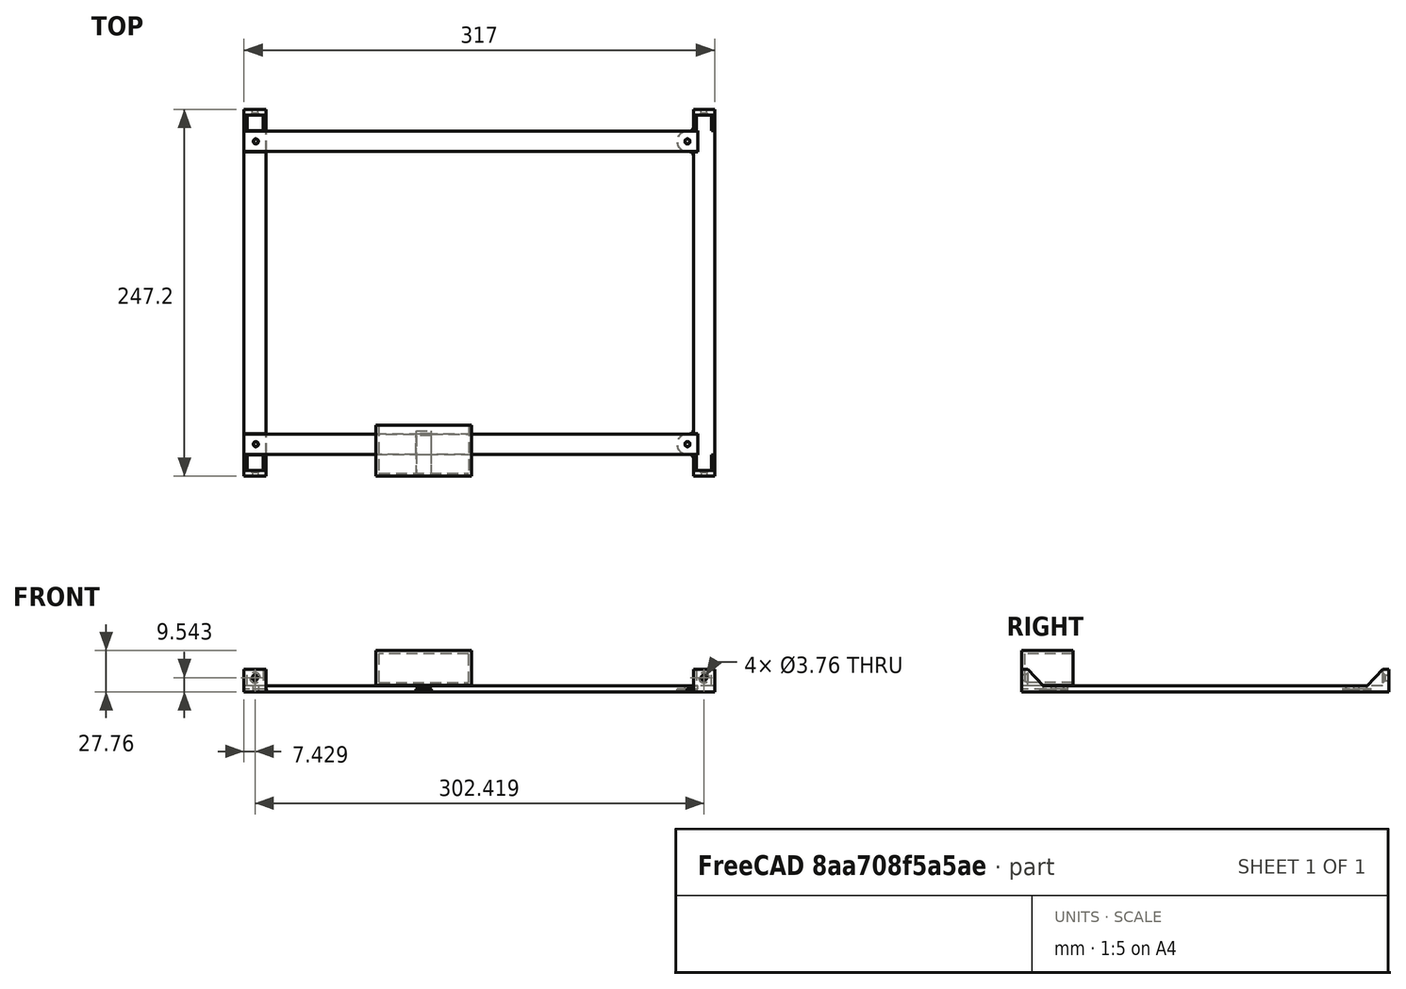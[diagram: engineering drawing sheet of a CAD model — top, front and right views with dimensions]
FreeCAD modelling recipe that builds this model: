
FCSTD DOCUMENT  (FreeCAD 1.0R39319 (Git))
Label: mounting
License: All rights reserved
LicenseURL: https://en.wikipedia.org/wiki/All_rights_reserved
objects: Sketcher::SketchObject×27, PartDesign::Pad×17, PartDesign::Hole×9, PartDesign::Body×5, TechDraw::DrawProjGroupItem×4, TechDraw::DrawViewDimension×3, PartDesign::Plane×2, PartDesign::Mirrored×2, Spreadsheet::Sheet×1, PartDesign::Pocket×1, TechDraw::DrawSVGTemplate×1, TechDraw::DrawProjGroup×1, TechDraw::DrawPage×1
note: 152 computed .brp shape members not serialized (recipe doc carries the construction recipe); baked Part::Feature solids carry a one-line shape summary decoded from their .brp

FEATURE [Spreadsheet::Sheet] Spreadsheet  label="Dimensions"
  cells = A1='Property; B1='value (mm); C1='description (left/right relative to FRONT OF SCREEN); A2='frame_inner_width; B2(frame_inner_width)=317.5; C2='Width of the inside of the frame, ie, width of the glass and matting.; A3='frame_inner_height; B3(frame_inner_height)=247.7; C3='Height of the inside of the frame, ie, height of the glass and matting.; A4='m2_insert_min_taper; B4(m2_insert_min_taper)=2.8; C4='The holes for the M2 heat set inserts are tapered. This is the diameter of the smallest part of the taper.; A5='m2_insert_max_taper; B5(m2_insert_max_taper)=3.2; C5='The holes for the M2 heat set inserts are tapered. This is the diameter of the largest part of the taper.; A6='m2_insert_space_around; B6(m2_insert_space_around)=5; C6='Space around the M2 heat set inserts.; A7='m2_insert_height; B7(m2_insert_height)=4; C7='Height of the M2 heat set insert.; A8='wood_screw_major_diameter; B8(wood_screw_major_diameter)=3.505; C8='The "major" diameter of the wood screws, used to mount the brackets to the frame.; A9='wood_screw_head_diameter; B9(wood_screw_head_diameter)=7.087; C9='The diameter of the wood screw's head.; A10='wood_screw_space_around; B10(wood_screw_space_around)=2; C10='The space around the wood screw's head.; A11='wood_screw_wall_thickness; B11(wood_screw_wall_thickness)=4; C11='Thickness of the wall that the wood screw goes through.; A12='battery_width; B12(battery_width)=60; C12='Width of the battery.; A13='battery_thickness; B13(battery_thickness)=19; C13='Battery thickness.; A14='battery_height; B14(battery_height)=65; C14='Height of the battery.; A15='tolerance; B15(tolerance)=0.254; C15='Tolerance. Makes holes bigger, and tabs smaller to accommodate inaccuracies.; A18='Don't change below this...; A19='inky_width; B19(inky_width)=296.7; C19='Width of Inky Impression 13.3".; A20='inky_height; B20(inky_height)=210; C20='Height of Inky Impression 13.3".; A21='screen_width; B21(screen_width)=270.4; C21='Width of the actual screen.; A22='screen_height; B22(screen_height)=202.8; C22='Height of the actual screen.; A23='screen_distance_to_left_side; B23(screen_distance_to_left_side)=8; C23='Distance from the left side of the Inky, looking from the front, to the left edge of the screen.; A24='screen_distance_to_right_side; B24(screen_distance_to_right_side)==inky_width - screen_distance_to_left_side - screen_width; C24='Distance from the right side of the Inky, looking from the front, to the right edge of the screen.; A25='screen_distance_to_top_side; B25(screen_distance_to_top_side)==(inky_height - screen_height) / 2; C25='Distance from the top side of the Inky to the top edge of the screen.; A26='screen_distance_to_bottom_side; B26(screen_distance_to_bottom_side)==inky_height - screen_height - screen_distance_to_top_side; C26='Distance from the bottom side of the Inky to the bottom edge of the screen.; A27='inky_mounting_hole_distance_to_edge; B27(inky_mounting_hole_distance_to_edge)=3; C27='Distance between the center of the mounting holes on the Inky, and the top/right/bottom/left edges of the Inky.; A28='inky_mounting_hole_to_frame_left; B28(inky_mounting_hole_to_frame_left)==(frame_inner_width - screen_width) / 2 - screen_distance_to_left_side + inky_mounting_hole_distance_to_edge - tolerance; C28='The horizontal distance between the left mounting holes and the left side of the frame (looking from the front).; A29='inky_mounting_hole_to_frame_right; B29(inky_mounting_hole_to_frame_right)==(frame_inner_width - screen_width) / 2 - screen_distance_to_right_side + inky_mounting_hole_distance_to_edge - tolerance; C29='The horizontal distance between the right mounting holes and the right side of the frame (looking from the front).; A30='inky_mounting_hole_to_frame_top; B30(inky_mounting_hole_to_frame_top)==(frame_inner_height - inky_height) / 2 - tolerance + inky_mounting_hole_distance_to_edge; C30='The vertical distance between the top mounting holes and the frame top.; A31='inky_mounting_hole_to_frame_bottom; B31(inky_mounting_hole_to_frame_bottom)==inky_mounting_hole_to_frame_top; C31='The vertical distance between the bottom mounting holes and the frame bottom.; A32='frame_left; B32(frame_left)==inky_width / 2 - inky_mounting_hole_distance_to_edge + inky_mounting_hole_to_frame_left; C32='The horizontal distance from the origin to the frame left.; A33='frame_right; B33(frame_right)==inky_width / 2 - inky_mounting_hole_distance_to_edge + inky_mounting_hole_to_frame_right; C33='The horizontal distance from the origin to the frame right.; A34='frame_top; B34(frame_top)==inky_height / 2 - inky_mounting_hole_distance_to_edge + inky_mounting_hole_to_frame_top; C34='The vertical distance from the origin to the frame top.; A35='frame_bottom; B35(frame_bottom)==inky_height / 2 - inky_mounting_hole_distance_to_edge + inky_mounting_hole_to_frame_bottom; C35='The vertical distance from the origin to the frame bottom.; A36='inky_button_clearance; B36(inky_button_clearance)=1; C36='The closest the bracket can be to the buttons on the side of the Inky.; A37='m2_insert_mid_taper; B37(m2_insert_mid_taper)==(m2_insert_min_taper + m2_insert_max_taper) / 2; C37='The mid-point of the M2 taper.; A38='top_of_bottom_bracket; B38(top_of_bottom_bracket)==inky_height / 2 - inky_mounting_hole_distance_to_edge - m2_insert_max_taper / 2 - tolerance - m2_insert_space_around; C38='Vertical distance between the top of the bottom bracket and the middle of the Inky.; A39='battery_clip_width; B39(battery_clip_width)=10; C39='Width of the battery clip.; A40='battery_holder_wall_thickness; B40(battery_holder_wall_thickness)=2; C40='Thickness of the battery holder's walls.; A41='battery_holder_bottom; B41(battery_holder_bottom)==min(frame_bottom; top_of_bottom_bracket - tolerance - battery_holder_wall_thickness + battery_height / 2 + battery_holder_wall_thickness); C41='Vertical distance to the bottom of the battery holder, relative to the middle of the Inky.
FEATURE [Sketcher::SketchObject] Sketch
  ArcFitTolerance = 1e-06
  AttachmentSupport = -> [XY_Plane001]
  FullyConstrained = true
  MakeInternals = false
  MapMode = 5
  expr: .Constraints.bracket_width = <<Dimensions>>.inky_mounting_hole_to_frame_left - <<Dimensions>>.inky_mounting_hole_distance_to_edge - <<Dimensions>>.inky_button_clearance
  expr: Constraints[39] = <<Dimensions>>.inky_mounting_hole_distance_to_edge
  expr: Constraints[40] = <<Dimensions>>.frame_inner_height - 2 * <<Dimensions>>.tolerance
  expr: Constraints[43] = <<Dimensions>>.inky_mounting_hole_to_frame_bottom - <<Dimensions>>.m2_insert_max_taper / 2 - <<Dimensions>>.tolerance - <<Dimensions>>.m2_insert_space_around - <<Dimensions>>.inky_mounting_hole_distance_to_edge
  expr: Constraints[44] = <<Dimensions>>.inky_mounting_hole_to_frame_top - <<Dimensions>>.m2_insert_max_taper / 2 - <<Dimensions>>.tolerance - <<Dimensions>>.m2_insert_space_around - <<Dimensions>>.inky_mounting_hole_distance_to_edge
  expr: Constraints[45] = <<Dimensions>>.inky_button_clearance
  expr: Constraints[46] = <<Dimensions>>.m2_insert_max_taper + 2 * <<Dimensions>>.tolerance + 2 * <<Dimensions>>.m2_insert_space_around
  expr: Constraints[47] = <<Dimensions>>.m2_insert_max_taper + 2 * <<Dimensions>>.tolerance + 2 * <<Dimensions>>.m2_insert_space_around
  expr: Constraints[50] = <<Dimensions>>.inky_width / 2 - <<Dimensions>>.inky_mounting_hole_distance_to_edge
  expr: Constraints[51] = <<Dimensions>>.inky_height / 2 - <<Dimensions>>.inky_mounting_hole_distance_to_edge
  sketch-geometry (21):
    g0: LineSegment StartX=149.35 StartY=-123.596 StartZ=0 EndX=163.646 EndY=-123.596 EndZ=0
    g1: LineSegment StartX=163.646 StartY=-123.596 StartZ=0 EndX=163.646 EndY=123.596 EndZ=0
    g2: LineSegment StartX=163.646 StartY=123.596 StartZ=0 EndX=149.35 EndY=123.596 EndZ=0
    g3: LineSegment StartX=149.35 StartY=123.596 StartZ=0 EndX=149.35 EndY=111.854 EndZ=0
    g4: ArcOfCircle CenterX=146.35 CenterY=111.854 CenterZ=0 NormalX=0 NormalY=0 NormalZ=1 AngleXU=0 Radius=3 StartAngle=4.71239 EndAngle=6.28319
    g5: LineSegment StartX=146.35 StartY=108.854 StartZ=0 EndX=145.35 EndY=108.854 EndZ=0
    g6: ArcOfCircle CenterX=145.35 CenterY=102 CenterZ=0 NormalX=0 NormalY=0 NormalZ=1 AngleXU=0 Radius=6.854 StartAngle=1.5708 EndAngle=4.71239
    g7: LineSegment StartX=145.35 StartY=95.146 StartZ=0 EndX=146.35 EndY=95.146 EndZ=0
    g8: ArcOfCircle CenterX=146.35 CenterY=92.146 CenterZ=0 NormalX=0 NormalY=0 NormalZ=1 AngleXU=0 Radius=3 StartAngle=1.6e-15 EndAngle=1.5708
    g9: LineSegment StartX=149.35 StartY=92.146 StartZ=0 EndX=149.35 EndY=-92.146 EndZ=0
    g10: ArcOfCircle CenterX=146.35 CenterY=-92.146 CenterZ=0 NormalX=0 NormalY=0 NormalZ=1 AngleXU=0 Radius=3 StartAngle=4.71239 EndAngle=6.28319
    g11: LineSegment StartX=146.35 StartY=-95.146 StartZ=0 EndX=145.35 EndY=-95.146 EndZ=0
    g12: ArcOfCircle CenterX=145.35 CenterY=-102 CenterZ=0 NormalX=0 NormalY=0 NormalZ=1 AngleXU=0 Radius=6.854 StartAngle=1.5708 EndAngle=4.71239
    g13: LineSegment StartX=145.35 StartY=-108.854 StartZ=0 EndX=146.35 EndY=-108.854 EndZ=0
    g14: ArcOfCircle CenterX=146.35 CenterY=-111.854 CenterZ=0 NormalX=0 NormalY=0 NormalZ=1 AngleXU=0 Radius=3 StartAngle=-5.24e-14 EndAngle=1.5708
    g15: LineSegment StartX=149.35 StartY=-111.854 StartZ=0 EndX=149.35 EndY=-123.596 EndZ=0
    g16: LineSegment [constr] StartX=149.35 StartY=-123.596 StartZ=0 EndX=149.35 EndY=123.596 EndZ=0
    g17: LineSegment [constr] StartX=149.35 StartY=-111.854 StartZ=0 EndX=146.35 EndY=-111.854 EndZ=0
    g18: LineSegment [constr] StartX=149.35 StartY=-92.146 StartZ=0 EndX=146.35 EndY=-92.146 EndZ=0
    g19: LineSegment [constr] StartX=149.35 StartY=92.146 StartZ=0 EndX=146.35 EndY=92.146 EndZ=0
    g20: LineSegment [constr] StartX=149.35 StartY=111.854 StartZ=0 EndX=146.35 EndY=111.854 EndZ=0
  constraints (52):
    c: Coincident(g1,g2)
    c: Parallel(g0,g2)
    c: Coincident(g2,g3)
    c: Parallel(g1,g3)
    c: Tangent(g3,g4) = 1.5708
    c: Parallel(g0,g5)
    c: Tangent(g5,g6) = -1.5708
    c: Parallel(g0,g7)
    c: Tangent(g7,g8) = 1.5708
    c: Parallel(g1,g9)
    c: Tangent(g9,g10) = 1.5708
    c: Parallel(g0,g11)
    c: Tangent(g11,g12) = -1.5708
    c: Parallel(g0,g13)
    c: Tangent(g13,g14) = 1.5708
    c: Coincident(g15,g0)
    c: Parallel(g1,g15)
    c: Tangent(g14,g15) = 1.5708
    c: Tangent(g12,g13) = -1.5708
    c: Tangent(g10,g11) = 1.5708
    c: Tangent(g8,g9) = 1.5708
    c: Tangent(g6,g7) = -1.5708
    c: Tangent(g4,g5) = 1.5708
    c: Coincident(g16,g0)
    c: Coincident(g16,g2)
    c: Parallel(g1,g16)
    c: Equal(g13,g11)
    c: Equal(g11,g7)
    c: Equal(g7,g5)
    c: Coincident(g17,g14)
    c: Coincident(g17,g14)
    c: Coincident(g18,g9)
    c: Coincident(g18,g10)
    c: Coincident(g19,g8)
    c: Coincident(g19,g8)
    c: Coincident(g20,g3)
    c: Coincident(g20,g4)
    c: Equal(g17,g18)
    c: Equal(g18,g19)
    c: Distance(g17,g17) = 3
    c: Distance(g1,g0) = 247.192
    c: Coincident(g1,g0)
    c: Distance(g0,g0) = 14.296  'bracket_width'
    c: Distance(g15,g15) = 11.742
    c: Distance(g3,g3) = 11.742
    c: Distance(g13,g13) = 1
    c: Diameter(g6) = 13.708
    c: Diameter(g12) = 13.708
    c: Perpendicular(g1,g0)
    c: Vertical(g1)
    c: DistanceX(g6) = 145.35
    c: DistanceY(g6) = 102
FEATURE [PartDesign::Pad] Pad
  Direction = (0,0,1)
  Length = 2
  Length2 = 10
  Profile = -> Sketch
  ReferenceAxis = -> Sketch [N_Axis]
  Refine = true
  Suppressed = false
  Type = 0
  expr: Length = <<Dimensions>>.m2_insert_height / 2
FEATURE [Sketcher::SketchObject] Sketch001
  ArcFitTolerance = 1e-06
  AttachmentSupport = -> [Pad]
  ExternalGeometry = -> [Pad]
  FullyConstrained = true
  MakeInternals = false
  MapMode = 5
  Placement = pos=(0,0,2) rot=(0,0,1;0rad)
  expr: Constraints[24] = <<Dimensions>>.tolerance
  expr: Constraints[25] = <<Dimensions>>.m2_insert_max_taper / 2 + <<Dimensions>>.tolerance + <<Dimensions>>.m2_insert_space_around + <<Dimensions>>.tolerance
  expr: Constraints[26] = <<Dimensions>>.m2_insert_max_taper + <<Dimensions>>.tolerance * 2 + <<Dimensions>>.m2_insert_space_around * 2 + <<Dimensions>>.tolerance * 2
  sketch-geometry (12):
    g0: LineSegment StartX=149.35 StartY=-123.596 StartZ=0 EndX=163.646 EndY=-123.596 EndZ=0
    g1: LineSegment StartX=163.646 StartY=-123.596 StartZ=0 EndX=163.646 EndY=123.596 EndZ=0
    g2: LineSegment StartX=163.646 StartY=123.596 StartZ=0 EndX=149.35 EndY=123.596 EndZ=0
    g3: LineSegment StartX=149.35 StartY=-109.108 StartZ=0 EndX=149.35 EndY=-123.596 EndZ=0
    g4: LineSegment StartX=149.35 StartY=-109.108 StartZ=0 EndX=152.458 EndY=-109.108 EndZ=0
    g5: LineSegment StartX=152.458 StartY=-109.108 StartZ=0 EndX=152.458 EndY=-94.892 EndZ=0
    g6: LineSegment StartX=152.458 StartY=-94.892 StartZ=0 EndX=149.35 EndY=-94.892 EndZ=0
    g7: LineSegment StartX=149.35 StartY=94.892 StartZ=0 EndX=149.35 EndY=-94.892 EndZ=0
    g8: LineSegment StartX=149.35 StartY=123.596 StartZ=0 EndX=149.35 EndY=109.108 EndZ=0
    g9: LineSegment StartX=149.35 StartY=94.892 StartZ=0 EndX=152.458 EndY=94.892 EndZ=0
    g10: LineSegment StartX=152.458 StartY=94.892 StartZ=0 EndX=152.458 EndY=109.108 EndZ=0
    g11: LineSegment StartX=152.458 StartY=109.108 StartZ=0 EndX=149.35 EndY=109.108 EndZ=0
  constraints (31):
    c: Coincident(g0,g1)
    c: Coincident(g1,g2)
    c: Coincident(g2,g8)
    c: Coincident(g3,g0)
    c: Parallel(g1,g3)
    c: Coincident(g3,g4)
    c: Parallel(g0,g4)
    c: Perpendicular(g4,g5) = 1.5708
    c: Coincident(g5,g6)
    c: Coincident(g6,g7)
    c: Parallel(g0,g6)
    c: Parallel(g1,g7)
    c: Parallel(g1,g8)
    c: Coincident(g7,g9)
    c: Parallel(g0,g9)
    c: Coincident(g9,g10)
    c: Parallel(g1,g10)
    c: Coincident(g10,g11)
    c: Coincident(g11,g8)
    c: Parallel(g0,g11)
    c: Coincident(g1,g-3)
    c: Coincident(g2,g-3)
    c: Coincident(g0,g-5)
    c: Coincident(g0,g-5)
    c: DistanceY(g-6,g8) = 0.254
    c: DistanceX(g-6,g10) = 7.108
    c: DistanceY(g10,g10) = 14.216
    c: Equal(g11,g9)
    c: Equal(g9,g6)
    c: Equal(g5,g10)
    c: Equal(g8,g3)
FEATURE [PartDesign::Pad] Pad001
  BaseFeature = -> Pad
  Direction = (0,0,1)
  Length = 2
  Length2 = 10
  Profile = -> Sketch001
  ReferenceAxis = -> Sketch001 [N_Axis]
  Refine = true
  Suppressed = false
  Type = 0
  expr: Length = <<Dimensions>>.m2_insert_height / 2
FEATURE [Sketcher::SketchObject] Sketch002
  ArcFitTolerance = 1e-06
  AttachmentSupport = -> [Pad001]
  ExternalGeometry = -> [Pad001]
  FullyConstrained = true
  MakeInternals = false
  MapMode = 5
  Placement = pos=(0,0,4) rot=(0,0,1;0rad)
  expr: .Constraints.thickness = <<Dimensions>>.wood_screw_wall_thickness
  expr: Constraints[6] = .Constraints.thickness
  sketch-geometry (8):
    g0: LineSegment StartX=149.35 StartY=-123.596 StartZ=0 EndX=163.646 EndY=-123.596 EndZ=0
    g1: LineSegment StartX=163.646 StartY=-123.596 StartZ=0 EndX=163.646 EndY=-119.596 EndZ=0
    g2: LineSegment StartX=163.646 StartY=-119.596 StartZ=0 EndX=149.35 EndY=-119.596 EndZ=0
    g3: LineSegment StartX=149.35 StartY=-119.596 StartZ=0 EndX=149.35 EndY=-123.596 EndZ=0
    g4: LineSegment StartX=149.35 StartY=123.596 StartZ=0 EndX=149.35 EndY=119.596 EndZ=0
    g5: LineSegment StartX=149.35 StartY=119.596 StartZ=0 EndX=163.646 EndY=119.596 EndZ=0
    g6: LineSegment StartX=163.646 StartY=119.596 StartZ=0 EndX=163.646 EndY=123.596 EndZ=0
    g7: LineSegment StartX=163.646 StartY=123.596 StartZ=0 EndX=149.35 EndY=123.596 EndZ=0
  constraints (20):
    c: Coincident(g0,g1)
    c: Coincident(g1,g2)
    c: Coincident(g2,g3)
    c: Coincident(g3,g0)
    c: Parallel(g0,g2)
    c: Parallel(g1,g3)
    c: Distance(g3,g3) = 4
    c: Coincident(g4,g5)
    c: Coincident(g5,g6)
    c: Coincident(g6,g7)
    c: Coincident(g7,g4)
    c: Parallel(g1,g4)
    c: Parallel(g1,g6)
    c: Parallel(g0,g5)
    c: Distance(g4,g4) = 4  'thickness'
    c: Perpendicular(g1,g0)
    c: Coincident(g0,g-5)
    c: Coincident(g6,g-3)
    c: Coincident(g4,g-3)
    c: Coincident(g0,g-5)
FEATURE [PartDesign::Pad] Pad002
  BaseFeature = -> Pad001
  Direction = (0,0,1)
  Length = 11.087
  Length2 = 10
  Profile = -> Sketch002
  ReferenceAxis = -> Sketch002 [N_Axis]
  Refine = true
  Suppressed = false
  Type = 0
  expr: Length = <<Dimensions>>.wood_screw_head_diameter + <<Dimensions>>.wood_screw_space_around * 2
FEATURE [Sketcher::SketchObject] Sketch003
  ArcFitTolerance = 1e-06
  AttachmentSupport = -> [Pad002]
  ExternalGeometry = -> [Pad002]
  FullyConstrained = true
  MakeInternals = false
  MapMode = 5
  Placement = pos=(149.35,-1.3962e-12,-7.465e-13) rot=(-0.57735,0.57735,0.57735;4.18879rad)
  sketch-geometry (6):
    g0: LineSegment StartX=-119.596 StartY=15.087 StartZ=0 EndX=-119.596 EndY=4 EndZ=0
    g1: LineSegment StartX=-119.596 StartY=4 StartZ=0 EndX=-109.108 EndY=4 EndZ=0
    g2: LineSegment StartX=-109.108 StartY=4 StartZ=0 EndX=-119.596 EndY=15.087 EndZ=0
    g3: LineSegment StartX=119.596 StartY=15.087 StartZ=0 EndX=109.108 EndY=4 EndZ=0
    g4: LineSegment StartX=109.108 StartY=4 StartZ=0 EndX=119.596 EndY=4 EndZ=0
    g5: LineSegment StartX=119.596 StartY=4 StartZ=0 EndX=119.596 EndY=15.087 EndZ=0
  constraints (12):
    c: Coincident(g-3,g0)
    c: Coincident(g0,g-4)
    c: Coincident(g0,g1)
    c: Coincident(g1,g-4)
    c: Coincident(g1,g2)
    c: Coincident(g2,g0)
    c: Coincident(g-5,g3)
    c: Coincident(g3,g-6)
    c: Coincident(g3,g4)
    c: Coincident(g4,g-6)
    c: Coincident(g4,g5)
    c: Coincident(g5,g3)
FEATURE [PartDesign::Pad] Pad003
  BaseFeature = -> Pad002
  Direction = (-1,9.2e-15,5e-15)
  Length = 2
  Length2 = 10
  Profile = -> Sketch003
  ReferenceAxis = -> Sketch003 [N_Axis]
  Refine = true
  Reversed = true
  Suppressed = false
  Type = 0
  expr: Length = min((<<Sketch>>.Constraints.bracket_width / mm - <<Dimensions>>.wood_screw_head_diameter - 2 * <<Dimensions>>.tolerance) / 2; 2)
FEATURE [PartDesign::Plane] DatumPlane  label="MidPlane"
  AttachmentOffset = pos=(0,0,-7.148) rot=(0,0,1;0rad)
  AttachmentSupport = -> [Pad003]
  Length = 269.427
  MapMode = 5
  Placement = pos=(156.498,-1.9286e-12,-6.299e-13) rot=(-0.57735,0.57735,0.57735;4.18879rad)
  ResizeMode = 0
  Width = 72.2347
  expr: .AttachmentOffset.Base.z = 0 mm - <<Sketch>>.Constraints.bracket_width / 2
FEATURE [PartDesign::Mirrored] Mirrored
  BaseFeature = -> Pad003
  MirrorPlane = -> DatumPlane
  Originals = -> [Pad003]
  Refine = true
  Suppressed = false
  TransformMode = 0
FEATURE [Sketcher::SketchObject] Sketch004
  ArcFitTolerance = 1e-06
  AttachmentSupport = -> [Mirrored]
  ExternalGeometry = -> [Mirrored]
  FullyConstrained = true
  MakeInternals = false
  MapMode = 5
  Placement = pos=(0,119.596,0) rot=(1,0,0;1.5708rad)
  expr: Constraints[0] = <<Dimensions>>.wood_screw_major_diameter + 2 * <<Dimensions>>.tolerance
  sketch-geometry (3):
    g0: Circle CenterX=156.498 CenterY=9.5435 CenterZ=0 NormalX=0 NormalY=0 NormalZ=1 AngleXU=0 Radius=2.0065
    g1: LineSegment [constr] StartX=151.35 StartY=15.087 StartZ=0 EndX=161.646 EndY=4 EndZ=0
    g2: LineSegment [constr] StartX=151.35 StartY=4 StartZ=0 EndX=161.646 EndY=15.087 EndZ=0
  constraints (7):
    c: Diameter(g0) = 4.013
    c: Coincident(g1,g-3)
    c: Coincident(g1,g-4)
    c: Coincident(g2,g-4)
    c: Coincident(g2,g-3)
    c: PointOnObject(g0,g1)
    c: PointOnObject(g0,g2)
FEATURE [Sketcher::SketchObject] Sketch008
  ArcFitTolerance = 1e-06
  AttachmentSupport = -> [XY_Plane]
  FullyConstrained = true
  MakeInternals = false
  MapMode = 5
  expr: .Constraints.bracket_width = <<Dimensions>>.inky_mounting_hole_to_frame_right + <<Dimensions>>.m2_insert_max_taper / 2 + <<Dimensions>>.tolerance + <<Dimensions>>.m2_insert_space_around
  expr: Constraints[11] = 0 - (<<Dimensions>>.inky_width / 2 - <<Dimensions>>.inky_mounting_hole_distance_to_edge + <<Dimensions>>.inky_mounting_hole_to_frame_right)
  expr: Constraints[6] = <<Dimensions>>.frame_inner_height - 2 * <<Dimensions>>.tolerance
  expr: Constraints[9] = <<Dimensions>>.inky_height / 2 - <<Dimensions>>.inky_mounting_hole_distance_to_edge + <<Dimensions>>.inky_mounting_hole_to_frame_top
  sketch-geometry (4):
    g0: LineSegment StartX=-153.346 StartY=-123.596 StartZ=0 EndX=-138.496 EndY=-123.596 EndZ=0
    g1: LineSegment StartX=-138.496 StartY=-123.596 StartZ=0 EndX=-138.496 EndY=123.596 EndZ=0
    g2: LineSegment StartX=-138.496 StartY=123.596 StartZ=0 EndX=-153.346 EndY=123.596 EndZ=0
    g3: LineSegment StartX=-153.346 StartY=123.596 StartZ=0 EndX=-153.346 EndY=-123.596 EndZ=0
  constraints (12):
    c: Coincident(g0,g1)
    c: Coincident(g1,g2)
    c: Coincident(g2,g3)
    c: Coincident(g3,g0)
    c: Parallel(g0,g2)
    c: Parallel(g1,g3)
    c: Distance(g3,g3) = 247.192
    c: Distance(g0,g0) = 14.85  'bracket_width'
    c: Perpendicular(g1,g0)
    c: DistanceY(g1) = 123.596
    c: Vertical(g3)
    c: DistanceX(g2) = -153.346
FEATURE [PartDesign::Pad] Pad004
  Direction = (0,0,1)
  Length = 2
  Length2 = 10
  Profile = -> Sketch008
  ReferenceAxis = -> Sketch008 [N_Axis]
  Refine = true
  Suppressed = false
  Type = 0
  expr: Length = <<Dimensions>>.m2_insert_height / 2
FEATURE [Sketcher::SketchObject] Sketch009
  ArcFitTolerance = 1e-06
  AttachmentSupport = -> [Pad004]
  ExternalGeometry = -> [Pad004]
  FullyConstrained = true
  MakeInternals = false
  MapMode = 5
  Placement = pos=(0,0,2) rot=(0,0,1;0rad)
  expr: Constraints[0] = <<Dimensions>>.m2_insert_mid_taper + 2 * <<Dimensions>>.tolerance
  expr: Constraints[1] = <<Dimensions>>.m2_insert_mid_taper + 2 * <<Dimensions>>.tolerance
  expr: Constraints[2] = <<Dimensions>>.inky_mounting_hole_to_frame_right
  expr: Constraints[3] = <<Dimensions>>.inky_mounting_hole_to_frame_top
  expr: Constraints[4] = <<Dimensions>>.inky_mounting_hole_to_frame_right
  expr: Constraints[5] = <<Dimensions>>.inky_mounting_hole_to_frame_bottom
  sketch-geometry (2):
    g0: Circle CenterX=-145.35 CenterY=102 CenterZ=0 NormalX=0 NormalY=0 NormalZ=1 AngleXU=0 Radius=1.754
    g1: Circle CenterX=-145.35 CenterY=-102 CenterZ=0 NormalX=0 NormalY=0 NormalZ=1 AngleXU=0 Radius=1.754
  constraints (6):
    c: Diameter(g1) = 3.508
    c: Diameter(g0) = 3.508
    c: DistanceX(g-3,g0) = 7.996
    c: DistanceY(g0,g-3) = 21.596
    c: DistanceX(g-4,g1) = 7.996
    c: DistanceY(g-4,g1) = 21.596
FEATURE [PartDesign::Hole] Hole002
  BaseFeature = -> Pad004
  CustomThreadClearance = 0
  Depth = 2
  DepthType = 0
  Diameter = 3.254
  DrillForDepth = false
  DrillPoint = 1
  DrillPointAngle = 118
  HoleCutCountersinkAngle = 90
  HoleCutCustomValues = false
  HoleCutDepth = 0
  HoleCutDiameter = 6.1
  HoleCutType = 0
  ModelThread = false
  Profile = -> Sketch009
  Refine = true
  Suppressed = false
  Tapered = true
  TaperedAngle = 87.1376
  ThreadClass = 0
  ThreadDepth = 2
  ThreadDepthType = 0
  ThreadDirection = 0
  ThreadFit = 0
  ThreadSize = 0
  ThreadType = 0
  Threaded = false
  UseCustomThreadClearance = false
  expr: Depth = <<Dimensions>>.m2_insert_height / 2
  expr: Diameter = <<Dimensions>>.m2_insert_mid_taper + <<Dimensions>>.tolerance
  expr: TaperedAngle = atan(<<Dimensions>>.m2_insert_height / abs(<<Dimensions>>.m2_insert_mid_taper - <<Dimensions>>.m2_insert_min_taper))
FEATURE [Sketcher::SketchObject] Sketch010
  ArcFitTolerance = 1e-06
  AttachmentSupport = -> [Hole002]
  ExternalGeometry = -> [Hole002]
  FullyConstrained = true
  MakeInternals = false
  MapMode = 5
  Placement = pos=(0,0,2) rot=(0,0,1;0rad)
  expr: Constraints[22] = <<Dimensions>>.inky_mounting_hole_to_frame_bottom - <<Dimensions>>.m2_insert_max_taper / 2 - <<Dimensions>>.tolerance - <<Dimensions>>.m2_insert_space_around - <<Dimensions>>.tolerance
  expr: Constraints[23] = <<Dimensions>>.inky_mounting_hole_to_frame_bottom + <<Dimensions>>.m2_insert_max_taper / 2 + <<Dimensions>>.tolerance + <<Dimensions>>.m2_insert_space_around + <<Dimensions>>.tolerance
  expr: Constraints[24] = <<Dimensions>>.inky_mounting_hole_to_frame_top - <<Dimensions>>.m2_insert_max_taper / 2 - <<Dimensions>>.tolerance - <<Dimensions>>.m2_insert_space_around - <<Dimensions>>.tolerance
  expr: Constraints[25] = <<Dimensions>>.inky_mounting_hole_to_frame_top + <<Dimensions>>.m2_insert_max_taper / 2 + <<Dimensions>>.tolerance + <<Dimensions>>.m2_insert_space_around + <<Dimensions>>.tolerance
  sketch-geometry (12):
    g0: LineSegment StartX=-153.346 StartY=123.596 StartZ=0 EndX=-153.346 EndY=109.108 EndZ=0
    g1: LineSegment StartX=-153.346 StartY=109.108 StartZ=0 EndX=-138.496 EndY=109.108 EndZ=0
    g2: LineSegment StartX=-138.496 StartY=109.108 StartZ=0 EndX=-138.496 EndY=123.596 EndZ=0
    g3: LineSegment StartX=-138.496 StartY=123.596 StartZ=0 EndX=-153.346 EndY=123.596 EndZ=0
    g4: LineSegment StartX=-153.346 StartY=94.892 StartZ=0 EndX=-153.346 EndY=-94.892 EndZ=0
    g5: LineSegment StartX=-153.346 StartY=-94.892 StartZ=0 EndX=-138.496 EndY=-94.892 EndZ=0
    g6: LineSegment StartX=-138.496 StartY=-94.892 StartZ=0 EndX=-138.496 EndY=94.892 EndZ=0
    g7: LineSegment StartX=-138.496 StartY=94.892 StartZ=0 EndX=-153.346 EndY=94.892 EndZ=0
    g8: LineSegment StartX=-153.346 StartY=-109.108 StartZ=0 EndX=-153.346 EndY=-123.596 EndZ=0
    g9: LineSegment StartX=-153.346 StartY=-123.596 StartZ=0 EndX=-138.496 EndY=-123.596 EndZ=0
    g10: LineSegment StartX=-138.496 StartY=-123.596 StartZ=0 EndX=-138.496 EndY=-109.108 EndZ=0
    g11: LineSegment StartX=-138.496 StartY=-109.108 StartZ=0 EndX=-153.346 EndY=-109.108 EndZ=0
  constraints (32):
    c: Coincident(g0,g1)
    c: Coincident(g1,g2)
    c: Coincident(g2,g3)
    c: Coincident(g3,g0)
    c: Vertical(g0)
    c: Vertical(g2)
    c: Horizontal(g1)
    c: Coincident(g4,g5)
    c: Coincident(g5,g6)
    c: Coincident(g6,g7)
    c: Coincident(g7,g4)
    c: Vertical(g4)
    c: Vertical(g6)
    c: Horizontal(g5)
    c: Horizontal(g7)
    c: Coincident(g8,g9)
    c: Coincident(g9,g10)
    c: Coincident(g10,g11)
    c: Coincident(g11,g8)
    c: Vertical(g8)
    c: Vertical(g10)
    c: Horizontal(g11)
    c: DistanceY(g10,g10) = 14.488
    c: DistanceY(g8,g4) = 28.704
    c: DistanceY(g2,g2) = 14.488
    c: DistanceY(g4,g0) = 28.704
    c: Coincident(g0,g-4)
    c: Coincident(g2,g-5)
    c: PointOnObject(g4,g-4)
    c: PointOnObject(g6,g-5)
    c: Coincident(g8,g-4)
    c: Coincident(g9,g-5)
FEATURE [PartDesign::Pad] Pad005
  BaseFeature = -> Hole002
  Direction = (0,0,1)
  Length = 2
  Length2 = 10
  Profile = -> Sketch010
  ReferenceAxis = -> Sketch010 [N_Axis]
  Refine = true
  Suppressed = false
  Type = 0
  expr: Length = <<Dimensions>>.m2_insert_height / 2
FEATURE [Sketcher::SketchObject] Sketch011
  ArcFitTolerance = 1e-06
  AttachmentSupport = -> [Pad005]
  ExternalGeometry = -> [Pad005]
  FullyConstrained = true
  MakeInternals = false
  MapMode = 5
  Placement = pos=(0,0,4) rot=(0,0,1;0rad)
  expr: .Constraints.thickness = <<Dimensions>>.wood_screw_wall_thickness
  sketch-geometry (4):
    g0: LineSegment StartX=-153.346 StartY=123.596 StartZ=0 EndX=-153.346 EndY=119.596 EndZ=0
    g1: LineSegment StartX=-153.346 StartY=119.596 StartZ=0 EndX=-138.496 EndY=119.596 EndZ=0
    g2: LineSegment StartX=-138.496 StartY=119.596 StartZ=0 EndX=-138.496 EndY=123.596 EndZ=0
    g3: LineSegment StartX=-138.496 StartY=123.596 StartZ=0 EndX=-153.346 EndY=123.596 EndZ=0
  constraints (11):
    c: Coincident(g0,g1)
    c: Coincident(g1,g2)
    c: Coincident(g2,g3)
    c: Coincident(g3,g0)
    c: Vertical(g0)
    c: Vertical(g2)
    c: Horizontal(g1)
    c: Horizontal(g3)
    c: Coincident(g0,g-3)
    c: PointOnObject(g1,g-4)
    c: DistanceY(g2,g2) = 4  'thickness'
FEATURE [PartDesign::Pad] Pad006
  BaseFeature = -> Pad005
  Direction = (0,0,1)
  Length = 11.087
  Length2 = 10
  Profile = -> Sketch011
  ReferenceAxis = -> Sketch011 [N_Axis]
  Refine = true
  Suppressed = false
  Type = 0
  expr: Length = <<Dimensions>>.wood_screw_head_diameter + <<Dimensions>>.wood_screw_space_around * 2
FEATURE [Sketcher::SketchObject] Sketch012
  ArcFitTolerance = 1e-06
  AttachmentSupport = -> [Pad006]
  ExternalGeometry = -> [Pad006]
  FullyConstrained = true
  MakeInternals = false
  MapMode = 5
  Placement = pos=(0,0,4) rot=(0,0,1;0rad)
  expr: Constraints[10] = <<Sketch011>>.Constraints.thickness
  sketch-geometry (4):
    g0: LineSegment StartX=-153.346 StartY=-123.596 StartZ=0 EndX=-138.496 EndY=-123.596 EndZ=0
    g1: LineSegment StartX=-138.496 StartY=-123.596 StartZ=0 EndX=-138.496 EndY=-119.596 EndZ=0
    g2: LineSegment StartX=-138.496 StartY=-119.596 StartZ=0 EndX=-153.346 EndY=-119.596 EndZ=0
    g3: LineSegment StartX=-153.346 StartY=-119.596 StartZ=0 EndX=-153.346 EndY=-123.596 EndZ=0
  constraints (11):
    c: Coincident(g0,g1)
    c: Coincident(g1,g2)
    c: Coincident(g2,g3)
    c: Coincident(g3,g0)
    c: Horizontal(g0)
    c: Horizontal(g2)
    c: Vertical(g1)
    c: Vertical(g3)
    c: Coincident(g0,g-4)
    c: PointOnObject(g1,g-3)
    c: DistanceY(g1,g1) = 4
FEATURE [PartDesign::Pad] Pad007
  BaseFeature = -> Pad006
  Direction = (0,0,1)
  Length = 11.087
  Length2 = 10
  Profile = -> Sketch012
  ReferenceAxis = -> Sketch012 [N_Axis]
  Refine = true
  Suppressed = false
  Type = 0
  expr: Length = <<Dimensions>>.wood_screw_head_diameter + <<Dimensions>>.wood_screw_space_around * 2
FEATURE [Sketcher::SketchObject] Sketch013
  ArcFitTolerance = 1e-06
  AttachmentSupport = -> [Pad007]
  ExternalGeometry = -> [Pad007]
  FullyConstrained = true
  MakeInternals = false
  MapMode = 5
  Placement = pos=(-138.496,0,1.787e-13) rot=(0.57735,0.57735,0.57735;2.0944rad)
  sketch-geometry (6):
    g0: LineSegment StartX=119.596 StartY=15.087 StartZ=0 EndX=109.108 EndY=4 EndZ=0
    g1: LineSegment StartX=109.108 StartY=4 StartZ=0 EndX=119.596 EndY=4 EndZ=0
    g2: LineSegment StartX=119.596 StartY=4 StartZ=0 EndX=119.596 EndY=15.087 EndZ=0
    g3: LineSegment StartX=-119.596 StartY=15.087 StartZ=0 EndX=-109.108 EndY=4 EndZ=0
    g4: LineSegment StartX=-109.108 StartY=4 StartZ=0 EndX=-119.596 EndY=4 EndZ=0
    g5: LineSegment StartX=-119.596 StartY=4 StartZ=0 EndX=-119.596 EndY=15.087 EndZ=0
  constraints (12):
    c: Coincident(g-3,g0)
    c: Coincident(g0,g-4)
    c: Coincident(g0,g1)
    c: Coincident(g1,g-4)
    c: Coincident(g1,g2)
    c: Coincident(g2,g0)
    c: Coincident(g-5,g3)
    c: Coincident(g3,g-6)
    c: Coincident(g3,g4)
    c: Coincident(g4,g-6)
    c: Coincident(g4,g5)
    c: Coincident(g5,g3)
FEATURE [PartDesign::Pad] Pad008
  BaseFeature = -> Pad007
  Direction = (1,0,-1.3e-15)
  Length = 2
  Length2 = 10
  Profile = -> Sketch013
  ReferenceAxis = -> Sketch013 [N_Axis]
  Refine = true
  Reversed = true
  Suppressed = false
  Type = 0
  expr: Length = min((<<Sketch008>>.Constraints.bracket_width / mm - <<Dimensions>>.wood_screw_head_diameter - 2 * <<Dimensions>>.tolerance) / 2; 2)
FEATURE [PartDesign::Plane] DatumPlane001
  AttachmentOffset = pos=(0,0,-7.425) rot=(0,0,1;0rad)
  AttachmentSupport = -> [Pad008]
  Length = 269.427
  MapMode = 5
  Placement = pos=(-145.921,-8e-16,3.564e-13) rot=(0.57735,0.57735,0.57735;2.0944rad)
  ResizeMode = 0
  Width = 72.2347
  expr: .AttachmentOffset.Base.z = 0 - <<Sketch008>>.Constraints.bracket_width / 2 mm
FEATURE [PartDesign::Mirrored] Mirrored001
  BaseFeature = -> Pad008
  MirrorPlane = -> DatumPlane001
  Originals = -> [Pad008]
  Refine = true
  Suppressed = false
  TransformMode = 0
FEATURE [Sketcher::SketchObject] Sketch014
  ArcFitTolerance = 1e-06
  AttachmentOffset = pos=(0,0,2) rot=(0,0,1;0rad)
  AttachmentSupport = -> [XY_Plane002]
  FullyConstrained = true
  MakeInternals = false
  MapMode = 5
  Placement = pos=(0,0,2) rot=(0,0,1;0rad)
  expr: .AttachmentOffset.Base.z = <<Dimensions>>.m2_insert_height / 2
  expr: Constraints[10] = <<Dimensions>>.inky_width / 2 - <<Dimensions>>.inky_mounting_hole_distance_to_edge + <<Dimensions>>.m2_insert_max_taper / 2 + <<Dimensions>>.tolerance + <<Dimensions>>.m2_insert_space_around
  expr: Constraints[11] = <<Dimensions>>.inky_width / 2 - <<Dimensions>>.inky_mounting_hole_distance_to_edge + <<Dimensions>>.inky_mounting_hole_to_frame_right
  expr: Constraints[8] = <<Dimensions>>.m2_insert_max_taper + 2 * <<Dimensions>>.tolerance + 2 * <<Dimensions>>.m2_insert_space_around
  expr: Constraints[9] = <<Dimensions>>.inky_height / 2 - <<Dimensions>>.inky_mounting_hole_distance_to_edge - <<Dimensions>>.m2_insert_max_taper / 2 - <<Dimensions>>.tolerance - <<Dimensions>>.m2_insert_space_around
  sketch-geometry (4):
    g0: LineSegment StartX=-153.346 StartY=108.854 StartZ=0 EndX=-153.346 EndY=95.146 EndZ=0
    g1: LineSegment StartX=-153.346 StartY=95.146 StartZ=0 EndX=152.204 EndY=95.146 EndZ=0
    g2: LineSegment StartX=152.204 StartY=95.146 StartZ=0 EndX=152.204 EndY=108.854 EndZ=0
    g3: LineSegment StartX=152.204 StartY=108.854 StartZ=0 EndX=-153.346 EndY=108.854 EndZ=0
  constraints (12):
    c: Coincident(g0,g1)
    c: Coincident(g1,g2)
    c: Coincident(g2,g3)
    c: Coincident(g3,g0)
    c: Vertical(g0)
    c: Vertical(g2)
    c: Horizontal(g1)
    c: Horizontal(g3)
    c: DistanceY(g2,g2) = 13.708
    c: DistanceY(g-1,g1) = 95.146
    c: DistanceX(g-1,g2) = 152.204
    c: DistanceX(g0,g-1) = 153.346
FEATURE [Sketcher::SketchObject] Sketch015
  ArcFitTolerance = 1e-06
  AttachmentSupport = -> [Mirrored001]
  ExternalGeometry = -> [Mirrored001]
  FullyConstrained = true
  MakeInternals = false
  MapMode = 5
  Placement = pos=(0,119.596,0) rot=(1,0,0;1.5708rad)
  expr: Constraints[5] = <<Dimensions>>.wood_screw_major_diameter + <<Dimensions>>.tolerance * 2
  sketch-geometry (3):
    g0: LineSegment [constr] StartX=-151.346 StartY=15.087 StartZ=0 EndX=-140.496 EndY=4 EndZ=0
    g1: LineSegment [constr] StartX=-151.346 StartY=4 StartZ=0 EndX=-140.496 EndY=15.087 EndZ=0
    g2: Circle CenterX=-145.921 CenterY=9.5435 CenterZ=0 NormalX=0 NormalY=0 NormalZ=1 AngleXU=0 Radius=2.0065
  constraints (7):
    c: Coincident(g0,g-3)
    c: Coincident(g0,g-4)
    c: Coincident(g1,g-4)
    c: Coincident(g1,g-3)
    c: PointOnObject(g2,g1)
    c: Diameter(g2) = 4.013
    c: PointOnObject(g2,g0)
FEATURE [PartDesign::Pad] Pad009
  Direction = (0,0,1)
  Length = 2
  Length2 = 10
  Profile = -> Sketch014
  ReferenceAxis = -> Sketch014 [N_Axis]
  Refine = true
  Suppressed = false
  Type = 0
  expr: Length = <<Dimensions>>.m2_insert_height / 2
FEATURE [Sketcher::SketchObject] Sketch017
  ArcFitTolerance = 1e-06
  AttachmentSupport = -> [Pad009]
  ExternalGeometry = -> [Pad009]
  FullyConstrained = true
  MakeInternals = false
  MapMode = 5
  Placement = pos=(0,0,2) rot=(1,0,0;3.14159rad)
  expr: Constraints[11] = <<Dimensions>>.m2_insert_max_taper / 2 + <<Dimensions>>.tolerance + <<Dimensions>>.m2_insert_space_around
  expr: Constraints[4] = <<Dimensions>>.m2_insert_max_taper / 2 + <<Dimensions>>.tolerance + <<Dimensions>>.m2_insert_space_around + <<Dimensions>>.tolerance
  expr: Constraints[5] = <<Dimensions>>.inky_mounting_hole_to_frame_right + <<Dimensions>>.m2_insert_max_taper / 2 + <<Dimensions>>.tolerance + <<Dimensions>>.m2_insert_space_around + <<Dimensions>>.tolerance
  sketch-geometry (5):
    g0: LineSegment StartX=145.096 StartY=-95.146 StartZ=0 EndX=-138.242 EndY=-95.146 EndZ=0
    g1: LineSegment StartX=-138.242 StartY=-108.854 StartZ=0 EndX=145.096 EndY=-108.854 EndZ=0
    g2: LineSegment StartX=-138.242 StartY=-95.146 StartZ=0 EndX=-138.242 EndY=-108.854 EndZ=0
    g3: ArcOfCircle CenterX=145.096 CenterY=-102 CenterZ=0 NormalX=0 NormalY=0 NormalZ=1 AngleXU=0 Radius=6.854 StartAngle=1.57079 EndAngle=4.71239
    g4: LineSegment [constr] StartX=145.096 StartY=-95.146 StartZ=0 EndX=145.096 EndY=-108.854 EndZ=0
  constraints (15):
    c: PointOnObject(g0,g-3)
    c: PointOnObject(g0,g-3)
    c: PointOnObject(g1,g-4)
    c: PointOnObject(g1,g-4)
    c: DistanceX(g0,g-3) = 7.108
    c: DistanceX(g-3,g0) = 15.104
    c: Coincident(g2,g0)
    c: Coincident(g2,g1)
    c: Vertical(g2)
    c: Coincident(g3,g0)
    c: Coincident(g3,g1)
    c: Radius(g3) = 6.854
    c: Coincident(g4,g0)
    c: Coincident(g4,g1)
    c: Vertical(g4)
FEATURE [PartDesign::Pad] Pad010
  BaseFeature = -> Pad009
  Direction = (0,0,-1)
  Length = 2
  Length2 = 10
  Profile = -> Sketch017
  ReferenceAxis = -> Sketch017 [N_Axis]
  Refine = true
  Suppressed = false
  Type = 0
  expr: Length = <<Dimensions>>.m2_insert_height / 2
FEATURE [Sketcher::SketchObject] Sketch018
  ArcFitTolerance = 1e-06
  AttachmentOffset = pos=(0,0,2) rot=(0,0,1;0rad)
  AttachmentSupport = -> [XY_Plane003]
  FullyConstrained = true
  MakeInternals = false
  MapMode = 5
  Placement = pos=(0,0,2) rot=(0,0,1;0rad)
  expr: .AttachmentOffset.Base.z = <<Dimensions>>.m2_insert_height / 2
  expr: Constraints[10] = <<Dimensions>>.inky_width / 2 - <<Dimensions>>.inky_mounting_hole_distance_to_edge + <<Dimensions>>.inky_mounting_hole_to_frame_right
  expr: Constraints[11] = 0 - <<Dimensions>>.top_of_bottom_bracket
  expr: Constraints[8] = <<Dimensions>>.m2_insert_max_taper + 2 * <<Dimensions>>.tolerance + 2 * <<Dimensions>>.m2_insert_space_around
  expr: Constraints[9] = <<Dimensions>>.inky_width / 2 - <<Dimensions>>.inky_mounting_hole_distance_to_edge + <<Dimensions>>.m2_insert_max_taper / 2 + <<Dimensions>>.tolerance + <<Dimensions>>.m2_insert_space_around
  sketch-geometry (4):
    g0: LineSegment StartX=-153.346 StartY=-95.146 StartZ=0 EndX=-153.346 EndY=-108.854 EndZ=0
    g1: LineSegment StartX=-153.346 StartY=-108.854 StartZ=0 EndX=152.204 EndY=-108.854 EndZ=0
    g2: LineSegment StartX=152.204 StartY=-108.854 StartZ=0 EndX=152.204 EndY=-95.146 EndZ=0
    g3: LineSegment StartX=152.204 StartY=-95.146 StartZ=0 EndX=-153.346 EndY=-95.146 EndZ=0
  constraints (12):
    c: Coincident(g0,g1)
    c: Coincident(g1,g2)
    c: Coincident(g2,g3)
    c: Coincident(g3,g0)
    c: Vertical(g0)
    c: Vertical(g2)
    c: Horizontal(g1)
    c: Horizontal(g3)
    c: DistanceY(g2,g2) = 13.708
    c: DistanceX(g-1,g2) = 152.204
    c: DistanceX(g0,g-1) = 153.346
    c: DistanceY(g2) = -95.146
FEATURE [PartDesign::Pad] Pad011
  Direction = (0,0,1)
  Length = 2
  Length2 = 10
  Profile = -> Sketch018
  ReferenceAxis = -> Sketch018 [N_Axis]
  Refine = true
  Suppressed = false
  Type = 0
  expr: Length = <<Dimensions>>.m2_insert_height / 2
FEATURE [Sketcher::SketchObject] Sketch019
  ArcFitTolerance = 1e-06
  AttachmentSupport = -> [Pad010]
  ExternalGeometry = -> [Pad010]
  FullyConstrained = true
  MakeInternals = false
  MapMode = 5
  Placement = pos=(0,0,4) rot=(0,0,1;0rad)
  expr: Constraints[0] = <<Dimensions>>.m2_insert_max_taper + <<Dimensions>>.tolerance * 2
  expr: Constraints[17] = <<Dimensions>>.m2_insert_max_taper / 2 + <<Dimensions>>.tolerance + <<Dimensions>>.m2_insert_space_around
  expr: Constraints[8] = <<Dimensions>>.inky_mounting_hole_to_frame_right
  expr: Constraints[9] = <<Dimensions>>.m2_insert_max_taper + <<Dimensions>>.tolerance * 2
  sketch-geometry (6):
    g0: Circle CenterX=-145.35 CenterY=102 CenterZ=0 NormalX=0 NormalY=0 NormalZ=1 AngleXU=0 Radius=1.854
    g1: LineSegment [constr] StartX=-145.35 StartY=108.854 StartZ=0 EndX=-145.35 EndY=102 EndZ=0
    g2: LineSegment [constr] StartX=-145.35 StartY=102 StartZ=0 EndX=-145.35 EndY=95.146 EndZ=0
    g3: Circle CenterX=145.35 CenterY=102 CenterZ=0 NormalX=0 NormalY=0 NormalZ=1 AngleXU=0 Radius=1.854
    g4: LineSegment [constr] StartX=145.35 StartY=102 StartZ=0 EndX=145.35 EndY=108.854 EndZ=0
    g5: LineSegment [constr] StartX=145.35 StartY=102 StartZ=0 EndX=145.35 EndY=95.146 EndZ=0
  constraints (18):
    c: Diameter(g0) = 3.708
    c: PointOnObject(g1,g-3)
    c: Coincident(g1,g0)
    c: Coincident(g2,g0)
    c: PointOnObject(g2,g-4)
    c: Vertical(g2)
    c: Vertical(g1)
    c: Equal(g1,g2)
    c: DistanceX(g-3,g1) = 7.996
    c: Diameter(g3) = 3.708
    c: Coincident(g4,g3)
    c: PointOnObject(g4,g-3)
    c: Vertical(g4)
    c: Coincident(g5,g3)
    c: PointOnObject(g5,g-4)
    c: Vertical(g5)
    c: Equal(g4,g5)
    c: DistanceX(g4,g-3) = 6.854
FEATURE [PartDesign::Hole] Hole003
  BaseFeature = -> Pad010
  CustomThreadClearance = 0
  Depth = 2
  DepthType = 0
  Diameter = 3.454
  DrillForDepth = false
  DrillPoint = 1
  DrillPointAngle = 118
  HoleCutCountersinkAngle = 90
  HoleCutCustomValues = false
  HoleCutDepth = 0
  HoleCutDiameter = 6.1
  HoleCutType = 0
  ModelThread = false
  Profile = -> Sketch019
  Refine = true
  Suppressed = false
  Tapered = true
  TaperedAngle = 87.1376
  ThreadClass = 0
  ThreadDepth = 2
  ThreadDepthType = 0
  ThreadDirection = 0
  ThreadFit = 0
  ThreadSize = 0
  ThreadType = 0
  Threaded = false
  UseCustomThreadClearance = false
  expr: Depth = <<Dimensions>>.m2_insert_height / 2
  expr: Diameter = <<Dimensions>>.m2_insert_max_taper + <<Dimensions>>.tolerance
  expr: TaperedAngle = atan(<<Dimensions>>.m2_insert_height / abs(<<Dimensions>>.m2_insert_max_taper - <<Dimensions>>.m2_insert_mid_taper))
FEATURE [PartDesign::Body] Body002  label="Top Bracket"
  AllowCompound = false
  Group = -> [Sketch014,Pad009,Sketch017,Pad010,Sketch019,Hole003]
  Origin = -> Origin002
  Tip = -> Hole003
FEATURE [Sketcher::SketchObject] Sketch020
  ArcFitTolerance = 1e-06
  AttachmentSupport = -> [Pad011]
  ExternalGeometry = -> [Pad011]
  FullyConstrained = true
  MakeInternals = false
  MapMode = 5
  Placement = pos=(0,0,2) rot=(1,0,0;3.14159rad)
  expr: Constraints[12] = <<Dimensions>>.battery_clip_width + 2 * <<Dimensions>>.tolerance
  expr: Constraints[17] = 0 - ((<<Dimensions>>.battery_width + 2 * <<Dimensions>>.tolerance + 2 * <<Dimensions>>.battery_holder_wall_thickness - <<Dimensions>>.battery_clip_width) / 2 - <<Dimensions>>.tolerance)
  expr: Constraints[23] = <<Dimensions>>.m2_insert_max_taper / 2 + <<Dimensions>>.tolerance + <<Dimensions>>.m2_insert_space_around
  expr: Constraints[4] = <<Dimensions>>.inky_mounting_hole_to_frame_right + <<Dimensions>>.m2_insert_max_taper / 2 + <<Dimensions>>.tolerance + <<Dimensions>>.m2_insert_space_around + <<Dimensions>>.tolerance
  expr: Constraints[5] = <<Dimensions>>.m2_insert_max_taper / 2 + <<Dimensions>>.tolerance + <<Dimensions>>.m2_insert_space_around + <<Dimensions>>.tolerance
  sketch-geometry (9):
    g0: LineSegment StartX=-37.508 StartY=108.854 StartZ=0 EndX=-138.242 EndY=108.854 EndZ=0
    g1: LineSegment StartX=145.096 StartY=108.854 StartZ=0 EndX=-27 EndY=108.854 EndZ=0
    g2: LineSegment StartX=-138.242 StartY=95.146 StartZ=0 EndX=-37.508 EndY=95.146 EndZ=0
    g3: LineSegment StartX=-27 StartY=95.146 StartZ=0 EndX=145.096 EndY=95.146 EndZ=0
    g4: LineSegment StartX=-37.508 StartY=108.854 StartZ=0 EndX=-37.508 EndY=95.146 EndZ=0
    g5: LineSegment StartX=-27 StartY=108.854 StartZ=0 EndX=-27 EndY=95.146 EndZ=0
    g6: LineSegment StartX=-138.242 StartY=108.854 StartZ=0 EndX=-138.242 EndY=95.146 EndZ=0
    g7: ArcOfCircle CenterX=145.096 CenterY=102 CenterZ=0 NormalX=0 NormalY=0 NormalZ=1 AngleXU=0 Radius=6.854 StartAngle=1.57079 EndAngle=4.71239
    g8: LineSegment [constr] StartX=145.096 StartY=108.854 StartZ=0 EndX=145.096 EndY=95.146 EndZ=0
  constraints (27):
    c: PointOnObject(g1,g-3)
    c: PointOnObject(g0,g-3)
    c: PointOnObject(g2,g-4)
    c: PointOnObject(g3,g-4)
    c: DistanceX(g-3,g0) = 15.104
    c: DistanceX(g1,g-3) = 7.108
    c: Coincident(g4,g0)
    c: Coincident(g4,g2)
    c: Vertical(g4)
    c: Coincident(g5,g1)
    c: Coincident(g5,g3)
    c: Vertical(g5)
    c: DistanceX(g0,g1) = 10.508
    c: Horizontal(g0)
    c: Horizontal(g1)
    c: Horizontal(g2)
    c: Horizontal(g3)
    c: DistanceX(g1) = -27
    c: Coincident(g6,g0)
    c: Coincident(g6,g2)
    c: Vertical(g6)
    c: Coincident(g7,g1)
    c: Coincident(g7,g3)
    c: Radius(g7) = 6.854
    c: Coincident(g8,g1)
    c: Coincident(g8,g3)
    c: Vertical(g8)
FEATURE [PartDesign::Pad] Pad012
  BaseFeature = -> Pad011
  Direction = (0,0,-1)
  Length = 2
  Length2 = 10
  Profile = -> Sketch020
  ReferenceAxis = -> Sketch020 [N_Axis]
  Refine = true
  Suppressed = false
  Type = 0
  expr: Length = <<Dimensions>>.m2_insert_height / 2
FEATURE [Sketcher::SketchObject] Sketch021
  ArcFitTolerance = 1e-06
  AttachmentSupport = -> [Pad012]
  ExternalGeometry = -> [Pad012]
  FullyConstrained = true
  MakeInternals = false
  MapMode = 5
  Placement = pos=(0,0,4) rot=(0,0,1;0rad)
  expr: Constraints[16] = <<Dimensions>>.m2_insert_max_taper + 2 * <<Dimensions>>.tolerance
  expr: Constraints[17] = <<Dimensions>>.m2_insert_max_taper / 2 + <<Dimensions>>.tolerance + <<Dimensions>>.m2_insert_space_around
  expr: Constraints[7] = <<Dimensions>>.m2_insert_max_taper + 2 * <<Dimensions>>.tolerance
  expr: Constraints[8] = <<Dimensions>>.inky_mounting_hole_to_frame_right
  sketch-geometry (6):
    g0: Circle CenterX=-145.35 CenterY=-102 CenterZ=0 NormalX=0 NormalY=0 NormalZ=1 AngleXU=0 Radius=1.854
    g1: LineSegment [constr] StartX=-145.35 StartY=-102 StartZ=0 EndX=-145.35 EndY=-95.146 EndZ=0
    g2: LineSegment [constr] StartX=-145.35 StartY=-102 StartZ=0 EndX=-145.35 EndY=-108.854 EndZ=0
    g3: Circle CenterX=145.35 CenterY=-102 CenterZ=0 NormalX=0 NormalY=0 NormalZ=1 AngleXU=0 Radius=1.854
    g4: LineSegment [constr] StartX=145.35 StartY=-102 StartZ=0 EndX=145.35 EndY=-95.146 EndZ=0
    g5: LineSegment [constr] StartX=145.35 StartY=-102 StartZ=0 EndX=145.35 EndY=-108.854 EndZ=0
  constraints (18):
    c: Coincident(g1,g0)
    c: PointOnObject(g1,g-3)
    c: Vertical(g1)
    c: Coincident(g2,g0)
    c: PointOnObject(g2,g-4)
    c: Vertical(g2)
    c: Equal(g2,g1)
    c: Diameter(g0) = 3.708
    c: DistanceX(g-3,g1) = 7.996
    c: Coincident(g4,g3)
    c: PointOnObject(g4,g-3)
    c: Vertical(g4)
    c: Coincident(g5,g3)
    c: PointOnObject(g5,g-4)
    c: Vertical(g5)
    c: Equal(g4,g5)
    c: Diameter(g3) = 3.708
    c: DistanceX(g4,g-3) = 6.854
FEATURE [PartDesign::Hole] Hole004
  BaseFeature = -> Pad012
  CustomThreadClearance = 0
  Depth = 2
  DepthType = 0
  Diameter = 3.454
  DrillForDepth = false
  DrillPoint = 1
  DrillPointAngle = 118
  HoleCutCountersinkAngle = 90
  HoleCutCustomValues = false
  HoleCutDepth = 0
  HoleCutDiameter = 6.1
  HoleCutType = 0
  ModelThread = false
  Profile = -> Sketch021
  Refine = true
  Suppressed = false
  Tapered = true
  TaperedAngle = 87.1376
  ThreadClass = 0
  ThreadDepth = 2
  ThreadDepthType = 0
  ThreadDirection = 0
  ThreadFit = 0
  ThreadSize = 0
  ThreadType = 0
  Threaded = false
  UseCustomThreadClearance = false
  expr: Depth = <<Dimensions>>.m2_insert_height / 2
  expr: Diameter = <<Dimensions>>.m2_insert_max_taper + <<Dimensions>>.tolerance
  expr: TaperedAngle = atan(<<Dimensions>>.m2_insert_height / abs(<<Dimensions>>.m2_insert_max_taper - <<Dimensions>>.m2_insert_mid_taper))
FEATURE [PartDesign::Body] Body003  label="Bottom Bracket"
  AllowCompound = false
  Group = -> [Sketch018,Pad011,Sketch020,Pad012,Sketch021,Hole004]
  Origin = -> Origin003
  Tip = -> Hole004
FEATURE [Sketcher::SketchObject] Sketch022
  ArcFitTolerance = 1e-06
  AttachmentOffset = pos=(0,0,123.596) rot=(0,0,1;0rad)
  AttachmentSupport = -> [XZ_Plane004]
  FullyConstrained = true
  MakeInternals = false
  MapMode = 5
  Placement = pos=(0,-123.596,2.74e-14) rot=(1,0,0;1.5708rad)
  expr: .AttachmentOffset.Base.z = <<Dimensions>>.inky_height / 2 - <<Dimensions>>.inky_mounting_hole_distance_to_edge + <<Dimensions>>.inky_mounting_hole_to_frame_bottom
  expr: Constraints[10] = <<Dimensions>>.m2_insert_height + <<Dimensions>>.tolerance
  expr: Constraints[8] = 0 - (<<Dimensions>>.battery_width + 2 * <<Dimensions>>.tolerance + 2 * <<Dimensions>>.battery_holder_wall_thickness)
  expr: Constraints[9] = <<Dimensions>>.battery_thickness + 2 * <<Dimensions>>.tolerance + 2 * <<Dimensions>>.battery_holder_wall_thickness
  sketch-geometry (4):
    g0: LineSegment StartX=0 StartY=27.762 StartZ=0 EndX=0 EndY=4.254 EndZ=0
    g1: LineSegment StartX=0 StartY=4.254 StartZ=0 EndX=-64.508 EndY=4.254 EndZ=0
    g2: LineSegment StartX=-64.508 StartY=4.254 StartZ=0 EndX=-64.508 EndY=27.762 EndZ=0
    g3: LineSegment StartX=-64.508 StartY=27.762 StartZ=0 EndX=0 EndY=27.762 EndZ=0
  constraints (12):
    c: Coincident(g0,g1)
    c: Coincident(g1,g2)
    c: Coincident(g2,g3)
    c: Coincident(g3,g0)
    c: Vertical(g0)
    c: Vertical(g2)
    c: Horizontal(g1)
    c: Horizontal(g3)
    c: DistanceX(g3,g3) = -64.508
    c: DistanceY(g2,g2) = 23.508
    c: DistanceY(g1) = 4.254
    c: DistanceX(g0) = 0
FEATURE [PartDesign::Pad] Pad013
  Direction = (0,-1,2e-16)
  Length = 34.5
  Length2 = 10
  Placement = pos=(0,0,0) rot=(1,0,0;1.5708rad)
  Profile = -> Sketch022
  ReferenceAxis = -> Sketch022 [N_Axis]
  Refine = true
  Reversed = true
  Suppressed = false
  Type = 0
  expr: Length = <<Dimensions>>.battery_holder_wall_thickness + <<Dimensions>>.battery_height / 2
FEATURE [Sketcher::SketchObject] Sketch023
  ArcFitTolerance = 1e-06
  AttachmentSupport = -> [Pad013]
  ExternalGeometry = -> [Pad013]
  FullyConstrained = true
  MakeInternals = false
  MapMode = 5
  Placement = pos=(0,-89.096,0) rot=(-1,0,0;1.5708rad)
  expr: Constraints[10] = <<Dimensions>>.battery_holder_wall_thickness
  expr: Constraints[11] = <<Dimensions>>.battery_holder_wall_thickness
  expr: Constraints[8] = <<Dimensions>>.battery_holder_wall_thickness
  expr: Constraints[9] = <<Dimensions>>.battery_holder_wall_thickness
  sketch-geometry (4):
    g0: LineSegment StartX=-2 StartY=-6.254 StartZ=0 EndX=-2 EndY=-25.762 EndZ=0
    g1: LineSegment StartX=-2 StartY=-25.762 StartZ=0 EndX=-62.508 EndY=-25.762 EndZ=0
    g2: LineSegment StartX=-62.508 StartY=-25.762 StartZ=0 EndX=-62.508 EndY=-6.254 EndZ=0
    g3: LineSegment StartX=-62.508 StartY=-6.254 StartZ=0 EndX=-2 EndY=-6.254 EndZ=0
  constraints (12):
    c: Coincident(g0,g1)
    c: Coincident(g1,g2)
    c: Coincident(g2,g3)
    c: Coincident(g3,g0)
    c: Vertical(g0)
    c: Vertical(g2)
    c: Horizontal(g1)
    c: Horizontal(g3)
    c: Distance(g-3,g3) = 2
    c: Distance(g-4,g1) = 2
    c: DistanceX(g-3,g2) = 2
    c: DistanceX(g0,g-4) = 2
FEATURE [PartDesign::Pocket] Pocket004
  BaseFeature = -> Pad013
  Direction = (0,-1,-2e-16)
  Length = 32.5
  Length2 = 5
  Placement = pos=(0,0,0) rot=(1,0,0;1.5708rad)
  Profile = -> Sketch023
  ReferenceAxis = -> Sketch023 [N_Axis]
  Refine = true
  Suppressed = false
  Type = 0
  expr: Length = <<Dimensions>>.battery_height / 2
FEATURE [Sketcher::SketchObject] Sketch024
  ArcFitTolerance = 1e-06
  AttachmentSupport = -> [Pocket004]
  ExternalGeometry = -> [Pocket004]
  FullyConstrained = true
  MakeInternals = false
  MapMode = 5
  Placement = pos=(0,9e-16,4.254) rot=(1,0,0;3.14159rad)
  expr: Constraints[10] = (<<Dimensions>>.battery_width + 2 * <<Dimensions>>.tolerance + 2 * <<Dimensions>>.battery_holder_wall_thickness - <<Dimensions>>.battery_clip_width) / 2
  expr: Constraints[11] = <<Dimensions>>.top_of_bottom_bracket - <<Dimensions>>.tolerance
  expr: Constraints[8] = <<Dimensions>>.battery_holder_wall_thickness
  expr: Constraints[9] = <<Dimensions>>.battery_clip_width
  sketch-geometry (4):
    g0: LineSegment StartX=-37.254 StartY=94.892 StartZ=0 EndX=-37.254 EndY=92.892 EndZ=0
    g1: LineSegment StartX=-37.254 StartY=92.892 StartZ=0 EndX=-27.254 EndY=92.892 EndZ=0
    g2: LineSegment StartX=-27.254 StartY=92.892 StartZ=0 EndX=-27.254 EndY=94.892 EndZ=0
    g3: LineSegment StartX=-27.254 StartY=94.892 StartZ=0 EndX=-37.254 EndY=94.892 EndZ=0
  constraints (12):
    c: Coincident(g0,g1)
    c: Coincident(g1,g2)
    c: Coincident(g2,g3)
    c: Coincident(g3,g0)
    c: Vertical(g0)
    c: Vertical(g2)
    c: Horizontal(g1)
    c: Horizontal(g3)
    c: DistanceY(g2,g2) = 2
    c: DistanceX(g1,g1) = 10
    c: DistanceX(g-3,g0) = 27.254
    c: DistanceY(g2) = 94.892
FEATURE [PartDesign::Pad] Pad014
  BaseFeature = -> Pocket004
  Direction = (0,0,-1)
  Length = 4.254
  Length2 = 10
  Placement = pos=(0,0,0) rot=(1,0,0;1.5708rad)
  Profile = -> Sketch024
  ReferenceAxis = -> Sketch024 [N_Axis]
  Refine = true
  Suppressed = false
  Type = 0
  expr: Length = <<Dimensions>>.m2_insert_height + <<Dimensions>>.tolerance
FEATURE [Sketcher::SketchObject] Sketch025
  ArcFitTolerance = 1e-06
  AttachmentSupport = -> [Pad014]
  ExternalGeometry = -> [Pad014]
  FullyConstrained = true
  MakeInternals = false
  MapMode = 5
  Placement = pos=(0,-94.892,0) rot=(1,0,0;1.5708rad)
  expr: Constraints[10] = <<Dimensions>>.m2_insert_height / 2 - <<Dimensions>>.tolerance
  sketch-geometry (4):
    g0: LineSegment StartX=-37.254 StartY=-9e-16 StartZ=0 EndX=-27.254 EndY=-9e-16 EndZ=0
    g1: LineSegment StartX=-27.254 StartY=-9e-16 StartZ=0 EndX=-27.254 EndY=1.746 EndZ=0
    g2: LineSegment StartX=-27.254 StartY=1.746 StartZ=0 EndX=-37.254 EndY=1.746 EndZ=0
    g3: LineSegment StartX=-37.254 StartY=1.746 StartZ=0 EndX=-37.254 EndY=-9e-16 EndZ=0
  constraints (11):
    c: Coincident(g0,g1)
    c: Coincident(g1,g2)
    c: Coincident(g2,g3)
    c: Coincident(g3,g0)
    c: Horizontal(g0)
    c: Horizontal(g2)
    c: Vertical(g1)
    c: Vertical(g3)
    c: Coincident(g0,g-3)
    c: PointOnObject(g1,g-4)
    c: DistanceY(g1,g1) = 1.746
FEATURE [PartDesign::Pad] Pad015
  BaseFeature = -> Pad014
  Direction = (0,-1,2e-16)
  Length = 28.704
  Length2 = 10
  Placement = pos=(0,0,0) rot=(1,0,0;1.5708rad)
  Profile = -> Sketch025
  ReferenceAxis = -> Sketch025 [N_Axis]
  Refine = true
  Suppressed = false
  Type = 0
  expr: Length = <<Dimensions>>.battery_holder_bottom - <<Dimensions>>.top_of_bottom_bracket + <<Dimensions>>.tolerance
FEATURE [Sketcher::SketchObject] Sketch026
  ArcFitTolerance = 1e-06
  AttachmentSupport = -> [Pad015]
  ExternalGeometry = -> [Pad015]
  FullyConstrained = true
  MakeInternals = false
  MapMode = 5
  Placement = pos=(-27.254,0,0) rot=(0.707107,0,0.707107;3.14159rad)
  sketch-geometry (6):
    g0: LineSegment StartX=1.746 StartY=94.892 StartZ=0 EndX=3 EndY=94.892 EndZ=0
    g1: LineSegment StartX=3 StartY=94.892 StartZ=0 EndX=4.254 EndY=94.892 EndZ=0
    g2: LineSegment StartX=4.254 StartY=94.892 StartZ=0 EndX=4.254 EndY=96.146 EndZ=0
    g3: LineSegment StartX=4.254 StartY=96.146 StartZ=0 EndX=3 EndY=94.892 EndZ=0
    g4: LineSegment StartX=1.746 StartY=94.892 StartZ=0 EndX=1.746 EndY=96.146 EndZ=0
    g5: LineSegment StartX=1.746 StartY=96.146 StartZ=0 EndX=3 EndY=94.892 EndZ=0
  constraints (14):
    c: Coincident(g0,g-3)
    c: Symmetric(g-3,g-3,g0)
    c: Coincident(g1,g0)
    c: Coincident(g1,g-3)
    c: Coincident(g1,g2)
    c: Vertical(g2)
    c: Coincident(g2,g3)
    c: Coincident(g3,g0)
    c: Coincident(g0,g4)
    c: Vertical(g4)
    c: Coincident(g4,g5)
    c: Coincident(g5,g0)
    c: Equal(g0,g4)
    c: Equal(g4,g2)
FEATURE [PartDesign::Pad] Pad016
  BaseFeature = -> Pad015
  Direction = (1,0,-2e-16)
  Length = 10
  Length2 = 10
  Placement = pos=(0,0,0) rot=(1,0,0;1.5708rad)
  Profile = -> Sketch026
  ReferenceAxis = -> Sketch026 [N_Axis]
  Refine = true
  Reversed = true
  Suppressed = false
  Type = 0
  expr: Length = <<Dimensions>>.battery_clip_width
FEATURE [PartDesign::Body] Body004  label="Battery Holder"
  AllowCompound = false
  Group = -> [Sketch022,Pad013,Sketch023,Pocket004,Sketch024,Pad014,Sketch025,Pad015,Sketch026,Pad016]
  Origin = -> Origin004
  Tip = -> Pad016
FEATURE [PartDesign::Hole] Hole005
  BaseFeature = -> Mirrored
  CustomThreadClearance = 0
  Depth = 4
  DepthType = 0
  Diameter = 3.759
  DrillForDepth = false
  DrillPoint = 1
  DrillPointAngle = 118
  HoleCutCountersinkAngle = 90
  HoleCutCustomValues = false
  HoleCutDepth = 0
  HoleCutDiameter = 7.087
  HoleCutType = 2
  ModelThread = false
  Profile = -> Sketch004
  Refine = true
  Suppressed = false
  Tapered = false
  TaperedAngle = 90
  ThreadClass = 0
  ThreadDepth = 4
  ThreadDepthType = 0
  ThreadDirection = 0
  ThreadFit = 0
  ThreadSize = 0
  ThreadType = 0
  Threaded = false
  UseCustomThreadClearance = false
  expr: Depth = <<Dimensions>>.wood_screw_wall_thickness
  expr: Diameter = <<Dimensions>>.wood_screw_major_diameter + <<Dimensions>>.tolerance
  expr: HoleCutDiameter = <<Dimensions>>.wood_screw_head_diameter
FEATURE [Sketcher::SketchObject] Sketch005
  ArcFitTolerance = 1e-06
  AttachmentSupport = -> [Hole005]
  ExternalGeometry = -> [Hole005]
  FullyConstrained = true
  MakeInternals = false
  MapMode = 5
  Placement = pos=(0,-119.596,0) rot=(0,0.707107,0.707107;3.14159rad)
  expr: Constraints[0] = <<Dimensions>>.wood_screw_major_diameter + 2 * <<Dimensions>>.tolerance
  sketch-geometry (3):
    g0: Circle CenterX=-156.498 CenterY=9.5435 CenterZ=0 NormalX=0 NormalY=0 NormalZ=1 AngleXU=0 Radius=2.0065
    g1: LineSegment [constr] StartX=-161.646 StartY=15.087 StartZ=0 EndX=-151.35 EndY=4 EndZ=0
    g2: LineSegment [constr] StartX=-161.646 StartY=4 StartZ=0 EndX=-151.35 EndY=15.087 EndZ=0
  constraints (7):
    c: Diameter(g0) = 4.013
    c: Coincident(g1,g-3)
    c: Coincident(g1,g-4)
    c: Coincident(g2,g-4)
    c: Coincident(g2,g-3)
    c: PointOnObject(g0,g1)
    c: PointOnObject(g0,g2)
FEATURE [PartDesign::Hole] Hole006
  BaseFeature = -> Hole005
  CustomThreadClearance = 0
  Depth = 4
  DepthType = 0
  Diameter = 3.759
  DrillForDepth = false
  DrillPoint = 1
  DrillPointAngle = 118
  HoleCutCountersinkAngle = 90
  HoleCutCustomValues = false
  HoleCutDepth = 0
  HoleCutDiameter = 7.087
  HoleCutType = 2
  ModelThread = false
  Profile = -> Sketch005
  Refine = true
  Suppressed = false
  Tapered = false
  TaperedAngle = 90
  ThreadClass = 0
  ThreadDepth = 4
  ThreadDepthType = 0
  ThreadDirection = 0
  ThreadFit = 0
  ThreadSize = 0
  ThreadType = 0
  Threaded = false
  UseCustomThreadClearance = false
  expr: Depth = <<Dimensions>>.wood_screw_wall_thickness
  expr: Diameter = <<Dimensions>>.wood_screw_major_diameter + <<Dimensions>>.tolerance
  expr: HoleCutDiameter = <<Dimensions>>.wood_screw_head_diameter
FEATURE [Sketcher::SketchObject] Sketch006
  ArcFitTolerance = 1e-06
  AttachmentSupport = -> [Hole006]
  ExternalGeometry = -> [Hole006]
  FullyConstrained = true
  MakeInternals = false
  MapMode = 5
  Placement = pos=(0,0,2) rot=(0,0,1;0rad)
  expr: Constraints[0] = <<Dimensions>>.m2_insert_mid_taper + 2 * <<Dimensions>>.tolerance
  sketch-geometry (3):
    g0: Circle CenterX=145.35 CenterY=-102 CenterZ=0 NormalX=0 NormalY=0 NormalZ=1 AngleXU=0 Radius=1.754
    g1: LineSegment [constr] StartX=145.35 StartY=-95.146 StartZ=0 EndX=145.35 EndY=-102 EndZ=0
    g2: LineSegment [constr] StartX=145.35 StartY=-108.854 StartZ=0 EndX=145.35 EndY=-102 EndZ=0
  constraints (7):
    c: Diameter(g0) = 3.508
    c: Coincident(g1,g-3)
    c: Coincident(g1,g0)
    c: Vertical(g1)
    c: Coincident(g2,g-4)
    c: Coincident(g2,g0)
    c: Equal(g1,g2)
FEATURE [PartDesign::Hole] Hole
  BaseFeature = -> Hole006
  CustomThreadClearance = 0
  Depth = 2
  DepthType = 0
  Diameter = 3.254
  DrillForDepth = false
  DrillPoint = 1
  DrillPointAngle = 118
  HoleCutCountersinkAngle = 90
  HoleCutCustomValues = false
  HoleCutDepth = 0
  HoleCutDiameter = 6.1
  HoleCutType = 0
  ModelThread = false
  Profile = -> Sketch006
  Refine = true
  Suppressed = false
  Tapered = true
  TaperedAngle = 87.1376
  ThreadClass = 0
  ThreadDepth = 2
  ThreadDepthType = 0
  ThreadDirection = 0
  ThreadFit = 0
  ThreadSize = 0
  ThreadType = 0
  Threaded = false
  UseCustomThreadClearance = false
  expr: Depth = <<Dimensions>>.m2_insert_height / 2
  expr: Diameter = <<Dimensions>>.m2_insert_mid_taper + <<Dimensions>>.tolerance
  expr: TaperedAngle = atan(<<Dimensions>>.m2_insert_height / abs(<<Dimensions>>.m2_insert_mid_taper - <<Dimensions>>.m2_insert_min_taper))
FEATURE [Sketcher::SketchObject] Sketch007
  ArcFitTolerance = 1e-06
  AttachmentSupport = -> [Hole]
  ExternalGeometry = -> [Hole]
  FullyConstrained = true
  MakeInternals = false
  MapMode = 5
  Placement = pos=(0,0,2) rot=(0,0,1;0rad)
  expr: Constraints[0] = <<Dimensions>>.m2_insert_mid_taper + 2 * <<Dimensions>>.tolerance
  sketch-geometry (3):
    g0: Circle CenterX=145.35 CenterY=102 CenterZ=0 NormalX=0 NormalY=0 NormalZ=1 AngleXU=0 Radius=1.754
    g1: LineSegment [constr] StartX=145.35 StartY=108.854 StartZ=0 EndX=145.35 EndY=102 EndZ=0
    g2: LineSegment [constr] StartX=145.35 StartY=102 StartZ=0 EndX=145.35 EndY=95.146 EndZ=0
  constraints (7):
    c: Diameter(g0) = 3.508
    c: Coincident(g1,g-3)
    c: Vertical(g1)
    c: Coincident(g2,g1)
    c: Coincident(g2,g-4)
    c: Equal(g1,g2)
    c: Coincident(g0,g1)
FEATURE [PartDesign::Hole] Hole001
  BaseFeature = -> Hole
  CustomThreadClearance = 0
  Depth = 2
  DepthType = 0
  Diameter = 3.254
  DrillForDepth = false
  DrillPoint = 1
  DrillPointAngle = 118
  HoleCutCountersinkAngle = 90
  HoleCutCustomValues = false
  HoleCutDepth = 0
  HoleCutDiameter = 6.1
  HoleCutType = 0
  ModelThread = false
  Profile = -> Sketch007
  Refine = true
  Suppressed = false
  Tapered = true
  TaperedAngle = 87.1376
  ThreadClass = 0
  ThreadDepth = 2
  ThreadDepthType = 0
  ThreadDirection = 0
  ThreadFit = 0
  ThreadSize = 0
  ThreadType = 0
  Threaded = false
  UseCustomThreadClearance = false
  expr: Depth = <<Dimensions>>.m2_insert_height / 2
  expr: Diameter = <<Dimensions>>.m2_insert_mid_taper + <<Dimensions>>.tolerance
  expr: TaperedAngle = atan(<<Dimensions>>.m2_insert_height / abs(<<Dimensions>>.m2_insert_mid_taper - <<Dimensions>>.m2_insert_min_taper))
FEATURE [PartDesign::Body] Body  label="Left Bracket"
  AllowCompound = false
  Group = -> [Sketch,Pad,Sketch001,Pad001,Sketch002,Pad002,Sketch003,Pad003,DatumPlane,Mirrored,Sketch004,Hole005,Sketch005,Hole006,Sketch006,Hole,Sketch007,Hole001]
  Origin = -> Origin001
  Tip = -> Hole001
FEATURE [PartDesign::Hole] Hole007
  BaseFeature = -> Mirrored001
  CustomThreadClearance = 0
  Depth = 4
  DepthType = 0
  Diameter = 3.759
  DrillForDepth = false
  DrillPoint = 1
  DrillPointAngle = 118
  HoleCutCountersinkAngle = 90
  HoleCutCustomValues = false
  HoleCutDepth = 0
  HoleCutDiameter = 7.087
  HoleCutType = 2
  ModelThread = false
  Profile = -> Sketch015
  Refine = true
  Suppressed = false
  Tapered = false
  TaperedAngle = 90
  ThreadClass = 0
  ThreadDepth = 4
  ThreadDepthType = 0
  ThreadDirection = 0
  ThreadFit = 0
  ThreadSize = 0
  ThreadType = 0
  Threaded = false
  UseCustomThreadClearance = false
  expr: Depth = <<Dimensions>>.wood_screw_wall_thickness
  expr: Diameter = <<Dimensions>>.wood_screw_major_diameter + <<Dimensions>>.tolerance
  expr: HoleCutDiameter = <<Dimensions>>.wood_screw_head_diameter
FEATURE [Sketcher::SketchObject] Sketch016
  ArcFitTolerance = 1e-06
  AttachmentSupport = -> [Hole007]
  ExternalGeometry = -> [Hole007]
  FullyConstrained = true
  MakeInternals = false
  MapMode = 5
  Placement = pos=(0,-119.596,0) rot=(0,0.707107,0.707107;3.14159rad)
  expr: Constraints[0] = <<Dimensions>>.wood_screw_major_diameter + 2 * <<Dimensions>>.tolerance
  sketch-geometry (3):
    g0: Circle CenterX=145.921 CenterY=9.5435 CenterZ=0 NormalX=0 NormalY=0 NormalZ=1 AngleXU=0 Radius=2.0065
    g1: LineSegment [constr] StartX=140.496 StartY=15.087 StartZ=0 EndX=151.346 EndY=4 EndZ=0
    g2: LineSegment [constr] StartX=140.496 StartY=4 StartZ=0 EndX=151.346 EndY=15.087 EndZ=0
  constraints (7):
    c: Diameter(g0) = 4.013
    c: Coincident(g1,g-3)
    c: Coincident(g1,g-4)
    c: Coincident(g2,g-4)
    c: Coincident(g2,g-3)
    c: PointOnObject(g0,g1)
    c: PointOnObject(g0,g2)
FEATURE [PartDesign::Hole] Hole008
  BaseFeature = -> Hole007
  CustomThreadClearance = 0
  Depth = 4
  DepthType = 0
  Diameter = 3.759
  DrillForDepth = false
  DrillPoint = 1
  DrillPointAngle = 118
  HoleCutCountersinkAngle = 90
  HoleCutCustomValues = false
  HoleCutDepth = 0
  HoleCutDiameter = 7.087
  HoleCutType = 2
  ModelThread = false
  Profile = -> Sketch016
  Refine = true
  Suppressed = false
  Tapered = false
  TaperedAngle = 90
  ThreadClass = 0
  ThreadDepth = 4
  ThreadDepthType = 0
  ThreadDirection = 0
  ThreadFit = 0
  ThreadSize = 0
  ThreadType = 0
  Threaded = false
  UseCustomThreadClearance = false
  expr: Depth = <<Dimensions>>.wood_screw_wall_thickness
  expr: Diameter = <<Dimensions>>.wood_screw_major_diameter + <<Dimensions>>.tolerance
  expr: HoleCutDiameter = <<Dimensions>>.wood_screw_head_diameter
FEATURE [PartDesign::Body] Body001  label="Right Bracket"
  AllowCompound = false
  Group = -> [Sketch008,Pad004,Sketch009,Hole002,Sketch010,Pad005,Sketch011,Pad006,Sketch012,Pad007,Sketch013,Pad008,DatumPlane001,Mirrored001,Sketch015,Hole007,Sketch016,Hole008]
  Origin = -> Origin
  Tip = -> Hole008
FEATURE [TechDraw::DrawSVGTemplate] Template
  EditableTexts = creator=Bob Matcuk; date_of_issue=1/4/26; document_type=Component Drawing; identification_number=DN; language_code=EN; part_material=PLA; revision_index=AAA; scale=1 : 1; sheet_number=1 / 1; title=Picture Frame Mounting Bracket
  Height = 297
  Orientation = 1
  Template = /Applications/FreeCAD.app/Contents/Resources/share/Mod/TechDraw/Templates/A3_Landscape_ISO5457_minimal.svg
  Width = 420
FEATURE [TechDraw::DrawProjGroupItem] View  label="Front"
  CoarseView = false
  Direction = (0,0,1)
  Focus = 100
  HardHidden = false
  IsoCount = 0
  IsoHidden = false
  IsoVisible = false
  LockPosition = true
  Perspective = false
  Rotation = 0
  RotationVector = (1,0,0)
  Scale = 0.7
  ScaleType = 2
  ScrubCount = 1
  SeamHidden = false
  SeamVisible = false
  SmoothHidden = false
  SmoothVisible = true
  Source = -> [Body004,Body,Body001,Body002,Body003]
  Type = 0
  X = 0
  XDirection = (1,0,0)
  Y = 0
FEATURE [TechDraw::DrawProjGroupItem] ProjItem  label="Right"
  CoarseView = false
  Direction = (1,0,1e-16)
  Focus = 100
  HardHidden = false
  IsoCount = 0
  IsoHidden = false
  IsoVisible = false
  LockPosition = false
  Perspective = false
  Rotation = 0
  RotationVector = (1,0,0)
  Scale = 0.7
  ScaleType = 0
  ScrubCount = 1
  SeamHidden = false
  SeamVisible = false
  SmoothHidden = false
  SmoothVisible = true
  Source = -> [Body004,Body,Body001,Body002,Body003]
  Type = 2
  X = 135.664
  XDirection = (1e-16,0,-1)
  Y = 0
FEATURE [TechDraw::DrawProjGroupItem] ProjItem001  label="Left"
  CoarseView = false
  Direction = (-1,0,1e-16)
  Focus = 100
  HardHidden = false
  IsoCount = 0
  IsoHidden = false
  IsoVisible = false
  LockPosition = false
  Perspective = false
  Rotation = 0
  RotationVector = (1,0,0)
  Scale = 0.7
  ScaleType = 0
  ScrubCount = 1
  SeamHidden = false
  SeamVisible = false
  SmoothHidden = false
  SmoothVisible = true
  Source = -> [Body004,Body,Body001,Body002,Body003]
  Type = 1
  X = -135.664
  XDirection = (1e-16,0,1)
  Y = 0
FEATURE [TechDraw::DrawProjGroup] ProjGroup
  Anchor = -> View
  AutoDistribute = true
  LockPosition = false
  ProjectionType = 1
  Rotation = 0
  Scale = 0.7
  ScaleType = 2
  Source = -> [Body004,Body,Body001,Body002,Body003]
  Views = -> [View,ProjItem,ProjItem001]
  X = 210
  Y = 178.5
  spacingX = 15
  spacingY = 15
FEATURE [TechDraw::DrawProjGroupItem] View001  label="Perspective"
  CoarseView = false
  Direction = (0.57735,0.57735,0.57735)
  Focus = 100
  HardHidden = false
  IsoCount = 0
  IsoHidden = false
  IsoVisible = false
  LockPosition = false
  Perspective = false
  Rotation = 0
  RotationVector = (1,0,0)
  Scale = 0.2
  ScaleType = 2
  ScrubCount = 1
  SeamHidden = false
  SeamVisible = false
  SmoothHidden = false
  SmoothVisible = true
  Source = -> [Body004,Body,Body001,Body002,Body003]
  Type = 0
  X = 54.7145
  XDirection = (0.707107,-5.7735e-07,-0.707106)
  Y = 60.7857
FEATURE [TechDraw::DrawViewDimension] Dimension
  AngleOverride = false
  Arbitrary = false
  ArbitraryTolerances = false
  BoxCorners = (2) [(-117.672,-92.097,0),(117.672,92.097,0)]
  EqualTolerance = true
  ExtensionAngle = 0
  FormatSpec = %.2w
  FormatSpecOverTolerance = %+.2w
  FormatSpecUnderTolerance = %+.2w
  Inverted = false
  LineAngle = 0
  LockPosition = false
  MeasureType = 1
  OverTolerance = 0
  References2D = -> [View]
  Rotation = 0
  ScaleType = 0
  TheoreticalExact = false
  Type = 1
  UnderTolerance = 0
  X = 0
  Y = 102.056
FEATURE [TechDraw::DrawViewDimension] Dimension001
  AngleOverride = false
  Arbitrary = false
  ArbitraryTolerances = false
  BoxCorners = (2) [(-10.4108,-92.097,0),(10.4108,92.097,0)]
  EqualTolerance = true
  ExtensionAngle = 0
  FormatSpec = %.2w
  FormatSpecOverTolerance = %+.2w
  FormatSpecUnderTolerance = %+.2w
  Inverted = false
  LineAngle = 0
  LockPosition = false
  MeasureType = 1
  OverTolerance = 0
  References2D = -> [ProjItem001]
  Rotation = 0
  ScaleType = 0
  TheoreticalExact = false
  Type = 2
  UnderTolerance = 0
  X = -22.6964
  Y = 0
FEATURE [TechDraw::DrawViewDimension] Dimension002
  AngleOverride = false
  Arbitrary = false
  ArbitraryTolerances = false
  BoxCorners = (2) [(-10.4108,-92.097,0),(10.4108,92.097,0)]
  EqualTolerance = true
  ExtensionAngle = 0
  FormatSpec = %.2w
  FormatSpecOverTolerance = %+.2w
  FormatSpecUnderTolerance = %+.2w
  Inverted = false
  LineAngle = 0
  LockPosition = false
  MeasureType = 1
  OverTolerance = 0
  References2D = -> [ProjItem]
  Rotation = 0
  ScaleType = 0
  TheoreticalExact = false
  Type = 1
  UnderTolerance = 0
  X = 0
  Y = -107.587
FEATURE [TechDraw::DrawPage] Page  label="Drawings"
  KeepUpdated = true
  NextBalloonIndex = 1
  ProjectionType = 0
  Template = -> Template
  Views = -> [ProjGroup,View001,Dimension,Dimension001,Dimension002]
